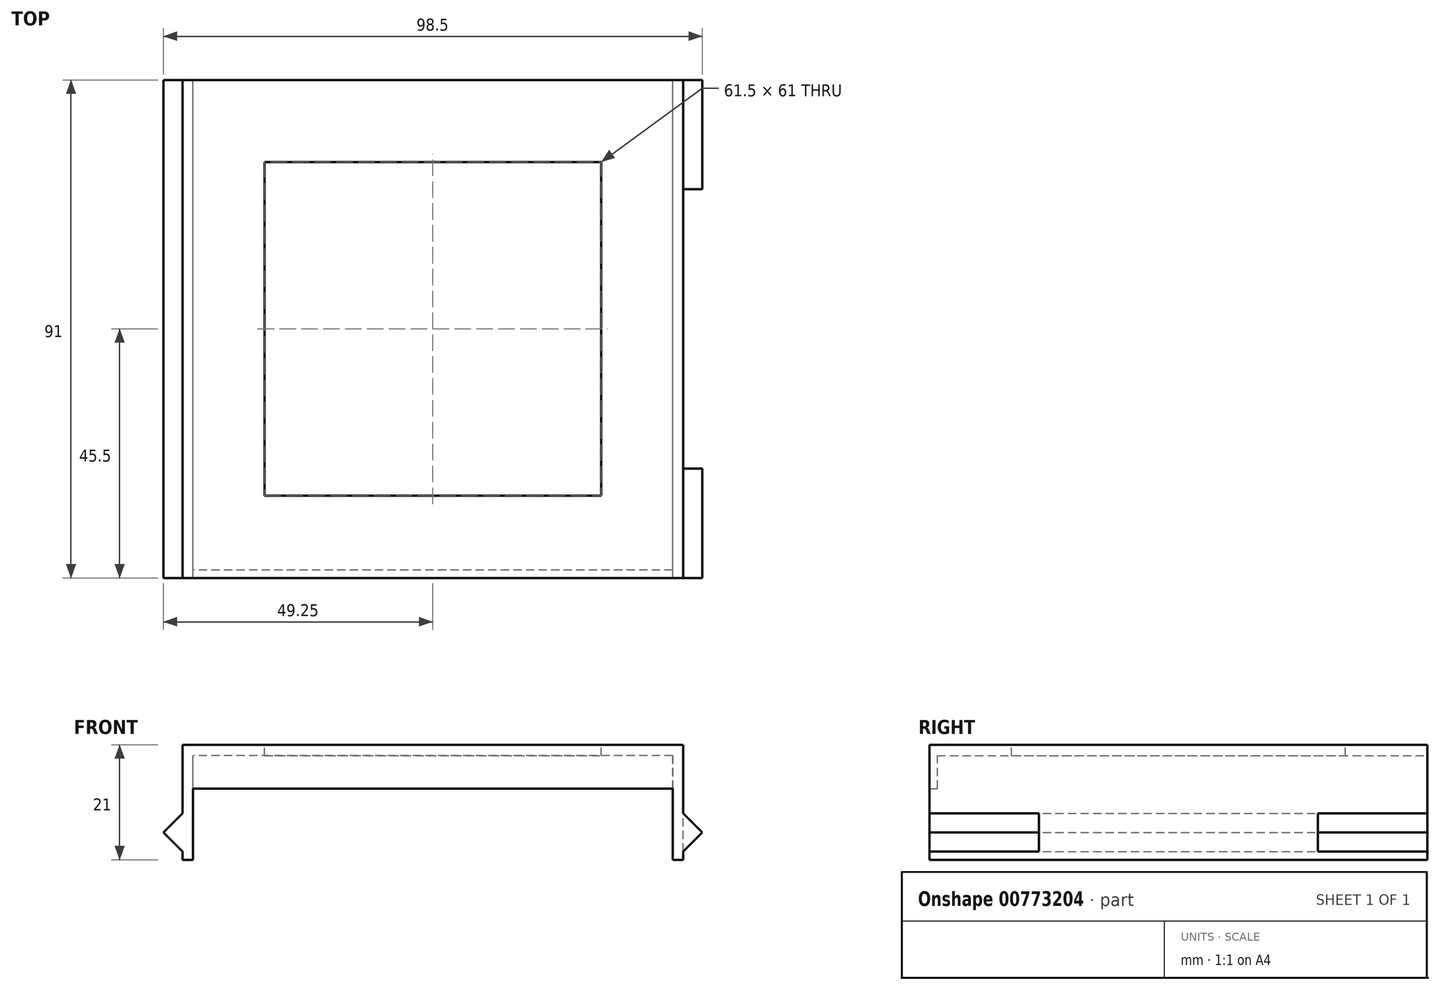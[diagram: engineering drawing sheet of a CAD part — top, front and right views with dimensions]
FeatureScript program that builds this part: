
annotation { "Feature Type Name" : "Feature", "Feature Type Description" : "" }
export const myFeature = defineFeature(function(context is Context, id is Id, definition is map)
    precondition{}
    {
        {
            var Q0;
            Q0=qCreatedBy(makeId("Front.planeOp"),FACE);
            var sketch = newSketch(context, id + "F0", { "sketchPlane" : qUnion([Q0])});
            skLineSegment(sketch, "E0", {"start": v(-45.75, 21) * mm, "end": v(-45.75, 8.5) * mm});
            skLineSegment(sketch, "E1", {"start": v(-45.75, 8.5) * mm, "end": v(-49.25, 5) * mm});
            skLineSegment(sketch, "E2", {"start": v(-49.25, 5) * mm, "end": v(-45.75, 1.5) * mm});
            skLineSegment(sketch, "E3", {"start": v(-45.75, 1.5) * mm, "end": v(-45.75, 0) * mm});
            skLineSegment(sketch, "E4", {"start": v(45.75, 0) * mm, "end": v(45.75, 1.5) * mm});
            skLineSegment(sketch, "E5", {"start": v(45.75, 1.5) * mm, "end": v(49.25, 5) * mm});
            skLineSegment(sketch, "E6", {"start": v(49.25, 5) * mm, "end": v(45.75, 8.5) * mm});
            skLineSegment(sketch, "E7", {"start": v(45.75, 8.5) * mm, "end": v(45.75, 21) * mm});
            skLineSegment(sketch, "E8", {"start": v(-45.75, 21) * mm, "end": v(45.75, 21) * mm});
            skLineSegment(sketch, "E9", {"start": v(-43.83, 0) * mm, "end": v(-43.83, 19) * mm});
            skLineSegment(sketch, "E10", {"start": v(-43.83, 19) * mm, "end": v(43.83, 19) * mm});
            skLineSegment(sketch, "E11", {"start": v(43.83, 19) * mm, "end": v(43.83, 0) * mm});
            skLineSegment(sketch, "E12", {"start": v(-45.75, 0) * mm, "end": v(-43.83, 0) * mm});
            skLineSegment(sketch, "E13", {"start": v(45.75, 0) * mm, "end": v(43.83, 0) * mm});
            skSolve(sketch);
        }
        {
            var Q0;
            Q0 = qSketchRegion(id + "F0", true);
            extrude(context, id + "F1", {"entities" : qUnion([Q0]), "endBound" : BoundingType.SYMMETRIC, "depth" : 91 * mm, "offsetDistance" : 25 * mm});
        }
        {
            var Q0;
            Q0=makeQuery(id+"F1.opExtrude","SWEPT_FACE",FACE,{"disambiguationData":[OSD([sQuery(id+"F0.wireOp",EDGE,"E8")])]});
            var sketch = newSketch(context, id + "F2", { "sketchPlane" : qUnion([Q0])});
            skLineSegment(sketch, "E14.0", {"start": v(-30.75, -30.5) * mm, "end": v(30.75, -30.5) * mm});
            skLineSegment(sketch, "E14.1", {"start": v(-30.75, -30.5) * mm, "end": v(-30.75, 30.5) * mm});
            skLineSegment(sketch, "E14.2", {"start": v(-30.75, 30.5) * mm, "end": v(30.75, 30.5) * mm});
            skLineSegment(sketch, "E14.3", {"start": v(30.75, -30.5) * mm, "end": v(30.75, 30.5) * mm});
            skSolve(sketch);
        }
        {
            var Q0;
            Q0=makeQuery(id+"F2.imprint","IMPRINT",FACE,{"disambiguationData":[TD([[makeQuery(id+"F2.imprint","IMPRINT",EDGE,{"derivedFrom":sQuery(id+"F2.wireOp",EDGE,"E14.0")}),1.0]])]});
            extrude(context, id + "F3", {"entities" : qUnion([Q0]), "operationType" : NewBodyOperationType.REMOVE, "endBound" : BoundingType.THROUGH_ALL, "oppositeDirection" : true, "depth" : 25 * mm, "offsetDistance" : 25 * mm});
        }
        {
            var Q0;
            Q0=makeQuery(id+"F1.opExtrude","SWEPT_FACE",FACE,{"disambiguationData":[OSD([sQuery(id+"F0.wireOp",EDGE,"E8")])]});
            var sketch = newSketch(context, id + "F4", { "sketchPlane" : qUnion([Q0])});
            skLineSegment(sketch, "E15.0", {"start": v(45.75, -45.5) * mm, "end": v(45.75, 45.5) * mm, "construction": true});
            skLineSegment(sketch, "E15.1", {"start": v(49.25, -45.5) * mm, "end": v(49.25, 45.5) * mm, "construction": true});
            skLineSegment(sketch, "E16", {"start": v(45.75, 25.5) * mm, "end": v(49.25, 25.5) * mm});
            skLineSegment(sketch, "E17", {"start": v(49.25, 25.5) * mm, "end": v(49.25, -25.5) * mm});
            skLineSegment(sketch, "E18", {"start": v(49.25, -25.5) * mm, "end": v(45.75, -25.5) * mm});
            skLineSegment(sketch, "E19", {"start": v(45.75, -25.5) * mm, "end": v(45.75, 25.5) * mm});
            skSolve(sketch);
        }
        {
            var Q0;
            Q0=makeQuery(id+"F4.imprint","IMPRINT",FACE,{"disambiguationData":[TD([[makeQuery(id+"F4.imprint","IMPRINT",EDGE,{"derivedFrom":sQuery(id+"F4.wireOp",EDGE,"E16")}),-1.0]])]});
            extrude(context, id + "F5", {"entities" : qUnion([Q0]), "operationType" : NewBodyOperationType.REMOVE, "endBound" : BoundingType.THROUGH_ALL, "oppositeDirection" : true, "depth" : 25 * mm, "offsetDistance" : 25 * mm});
        }
        {
            var Q0;
            Q0=makeQuery(id+"F1.opExtrude","SWEPT_FACE",FACE,{"disambiguationData":[OSD([sQuery(id+"F0.wireOp",EDGE,"E10")])]});
            var sketch = newSketch(context, id + "F6", { "sketchPlane" : qUnion([Q0])});
            skLineSegment(sketch, "E20.bottom", {"start": v(43.83, 45.5) * mm, "end": v(-43.83, 45.5) * mm});
            skLineSegment(sketch, "E20.top", {"start": v(43.83, 44.06) * mm, "end": v(-43.83, 44.06) * mm});
            skLineSegment(sketch, "E20.left", {"start": v(43.83, 45.5) * mm, "end": v(43.83, 44.06) * mm});
            skLineSegment(sketch, "E20.right", {"start": v(-43.83, 45.5) * mm, "end": v(-43.83, 44.06) * mm});
            skSolve(sketch);
        }
        {
            var Q0;
            Q0=makeQuery(id+"F6.imprint","IMPRINT",FACE,{"disambiguationData":[TD([[makeQuery(id+"F6.imprint","IMPRINT",EDGE,{"derivedFrom":sQuery(id+"F6.wireOp",EDGE,"E20.bottom")}),-1.0]])]});
            extrude(context, id + "F7", {"entities" : qUnion([Q0]), "operationType" : NewBodyOperationType.ADD, "depth" : 6 * mm, "offsetDistance" : 25 * mm});
        }
    });
